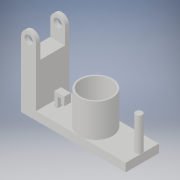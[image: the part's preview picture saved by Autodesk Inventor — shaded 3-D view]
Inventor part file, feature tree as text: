
AUTODESK INVENTOR PART (.ipt)
format: ipt  version: 2019 (Build 230136000, 136)  size: 180,224 bytes
history: native  units: in
note: dims shown in document units (in); Inventor stores cm internally (conversion verified against a paired STEP export)
features: sketch x7, extrude x6
ambient origin geometry x8: Origin, YZ Plane, XZ Plane, XY Plane, X Axis, Y Axis, Z Axis, Center Point
bodies: Solid1 (feature_tree)
feature tree (13):
  extrude  "Extrusion1"  Depth=0.1969in
  sketch  "Sketch2"  dims[d6=0.1772in d7=0.1969in]
  sketch  "Sketch6"  dims[d8=0.3543in d9=2.126in]
  extrude  "Extrusion5"  Depth=0.1969in
  sketch  "Sketch8"  dims[d13=0.2559in d14=0.7874in]
  extrude  "Extrusion6"  Depth=2.126in
  extrude  "Extrusion7"  Depth=0.1181in
  extrude  "Extrusion8"  Depth=0.7874in
  extrude  "Extrusion9"  Depth=0.3937in
  sketch  "Sketch1"  dims[d0=1.5748in d2=0.1969in]
  sketch  "Sketch7"  dims[d10=0.7874in d11=0.0in d12=0.1181in]
  sketch  "Sketch9"  dims[d16=1.0236in d19=0.3937in]
  sketch  "Sketch10"  dims[d20=0.1575in d21=0.3937in d22=0.5512in d40=0.5512in d41=0.5512in d42=0.5906in d43=0.5512in d44=0.0in d47=1.2795in d48=0.7874in d49=0.0in d50=0.7087in d51=0.9843in d52=0.0in d53=0.2362in d54=0.1575in d55=0.315in d56=0.1181in d57=0.315in d58=0.0in d59=0.0787in d60=0.0787in d61=0.2362in d62=0.1181in d63=0.1575in d64=0.0in]
